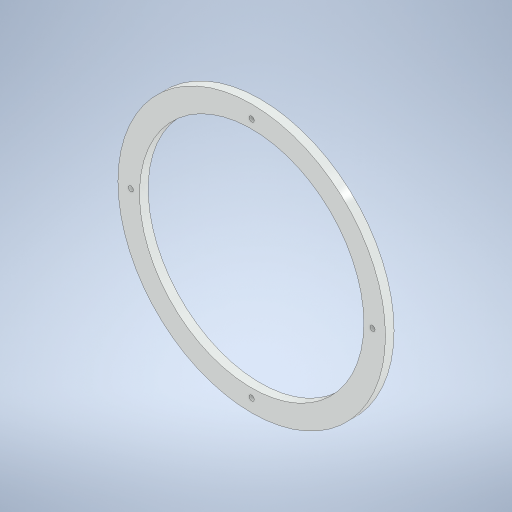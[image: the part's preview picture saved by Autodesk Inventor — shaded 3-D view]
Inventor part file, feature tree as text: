
AUTODESK INVENTOR PART (.ipt)
format: ipt  version: 2023.1 (Build 271208000, 208)  size: 257,024 bytes
history: native  units: mm
features: extrude x2, sketch x2, other x1
ambient origin geometry x8: Origin, YZ Plane, XZ Plane, XY Plane, X Axis, Y Axis, Z Axis, Center Point
bodies: Body1 (feature_tree)
feature tree (5):
  other  "솔리드1"
  extrude  "돌출1"  Depth=155.0mm
  extrude  "돌출2"  Depth=130.0mm
  sketch  "스케치1"
  sketch  "스케치2"
